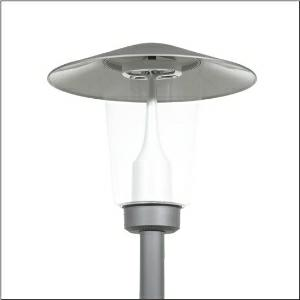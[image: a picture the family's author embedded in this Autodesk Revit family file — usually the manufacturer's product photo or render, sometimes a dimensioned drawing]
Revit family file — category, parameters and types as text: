
# Revit family: pilzleuchte_iq___p1_0a_5xa5235ff14hp_c3dc
name_source: partatom
category: Lighting Fixtures
units: mm (PartAtom-declared; Revit-internal decimal feet)

## family parameters
Cut with Voids When Loaded = No
Host = Face
Light Source = No
Part Type = Normal
Room Calculation Point = No
Round Connector Dimension = Use Diameter
Shared = No

## types (1)
- --- (1 x LED, 4740 lm, 33.6 W, 3000K)
    Apparent Load = 34 VA
    CIE Flux Codes = 35 64 90 96 100
    Color Rendering = 70
    Color Temperature = 3000K
    Default Elevation = 1800 mm
    Description = Mushroom Luminaire iQ, mast luminaire, Module 540 iQ-SR, primary light control with 3 zone facetted reflector, of plastic, silver coated, highly specular, structured, primary optical cover: cover, of PMMA, transparent, light distribution: P1.0a, light emission: direct distribution, primary light characteristic: strongly asymmetric, installation type: post-top, LED, High Power LED, rated luminous flux: 4.740lm, luminous efficacy: 141lm/W, light colour: 730, colour temperature: 3000K, control gear: iQ Street-Remote, control: pre-setting: logarithmic dimming characteristic, Street-Remote, Auto-Match, Temp-Guard, Lumen-Switch, Night-Set, Smart-Wire, Light-Fading, Desk-Remote (wireless, voltage-free reading and setting of iQ features in the workshop via application-optimized NFC function/RFID function), optimised constant luminous flux control (CLO 2.0), with terminal, 6-pole, max. 2.5mm², mains connection: 230..240V, AC, 50/60Hz, start of lifetime: 34W, end of service life: 36W, reduction: 15W, luminaire housing, upper part, of glass-fibre reinforced polyester, coated, Siteco® metallic grey (DB 702S), diameter: 650mm, height: 586mm, spigot size: d x l = 76 x 70mm (post-top) | with reducer (optional accessory) 60 x 70mm, mounting height: 3..5m, post-top mast mounting element, of diecast aluminium, coated, Siteco® metallic grey (DB 702S), Module 540 iQ-SR, traffic white (RAL 9016), equipment: Power, protection rating (complete): IP65, insulation class (complete): insulation class II (safety insulation), certification: CE, ENEC, VDE, packaging unit: 1 piece

Light Distribution: P1.0a
    Height = 586 mm
    Lamp = 1 x LED
    Lamp Light Flux = 4740 lm
    Lamp Power = 33.6 W
    Lamp count = 1
    Length = 650 mm
    Luminous efficacy = 141 lm/W
    Manufacturer = Siteco
    ModVariant = No
    Model = 5XA5235FF14HP
    Number of Poles = 1
    OnlyDefault = Yes
    Power Factor = 1
    Product Name = Pilzleuchte iQ | P1.0a
    Product group = mast luminaire | pylon top
    ProductGroupID = 6100
    Protection Class = Protection class II
    Protection Degree = IP 65
    RLX_Detail_Level = 1
    RLX_Emergency_Light_Flux = 0 lm
    RLX_Emergency_Type = 0
    RLX_Emergency_Type_DB = No
    RlxData = <blob elided: 52333 chars, md5=78c64598>
    Socket = socket
    Standby Power = 0 W
    System Light Flux = 4740 lm
    System Power = 34 W
    Type Comments = factory setting: luminous flux: 100 % | dim-lin: 254 | 695 mA
    Type Image = l_1006077.jpg
    URL = http://relux.com
    VarID = @adj_192144
    Voltage = 0 V
    Weight = 0.00 kg
    Width = 0 mm  [stored 0 ft]

note: [stored X ft] marks values corroborated as IEEE doubles in the binary element streams (Revit-internal decimal feet)

## geometry (parser evidence)
native form markers: Blend x4, Sweep x11
no freeform markers — native parametric forms only
